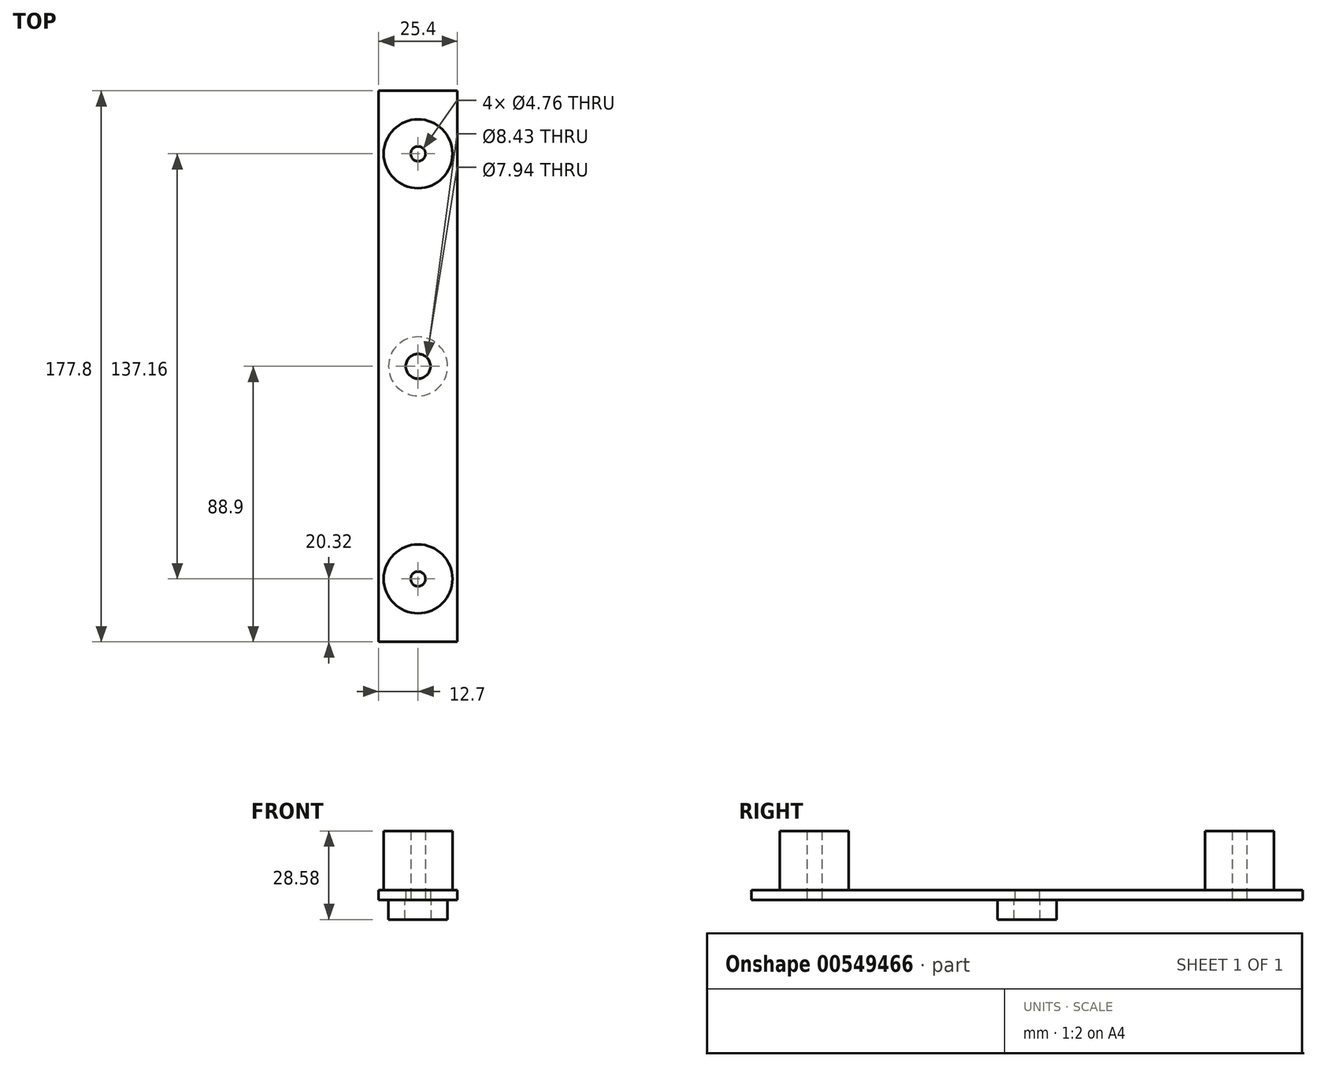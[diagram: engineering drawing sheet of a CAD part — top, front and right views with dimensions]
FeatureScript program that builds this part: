
annotation { "Feature Type Name" : "Feature", "Feature Type Description" : "" }
export const myFeature = defineFeature(function(context is Context, id is Id, definition is map)
    precondition{}
    {
        {
            var Q0;
            Q0=qCreatedBy(makeId("Top.planeOp"),FACE);
            var sketch = newSketch(context, id + "F0", { "sketchPlane" : qUnion([Q0])});
            skLineSegment(sketch, "E0.bottom", {"start": v(-12.7, 88.9) * mm, "end": v(12.7, 88.9) * mm});
            skLineSegment(sketch, "E0.top", {"start": v(-12.7, -88.9) * mm, "end": v(12.7, -88.9) * mm});
            skLineSegment(sketch, "E0.left", {"start": v(-12.7, 88.9) * mm, "end": v(-12.7, -88.9) * mm});
            skLineSegment(sketch, "E0.right", {"start": v(12.7, 88.9) * mm, "end": v(12.7, -88.9) * mm});
            skPoint(sketch, "E0.middle", {"position": v(0, 0) * mm});
            skPoint(sketch, "E1", {"position": v(0, -68.58) * mm});
            skPoint(sketch, "E2.MirrorP", {"position": v(0, 68.58) * mm});
            skCircle(sketch, "E3", {"center": v(0, -68.58) * mm, "radius": 2.38 * mm});
            skCircle(sketch, "E4.MirrorC", {"center": v(0, 68.58) * mm, "radius": 2.38 * mm});
            skCircle(sketch, "E5", {"center": v(0, 0) * mm, "radius": 3.97 * mm});
            skSolve(sketch);
        }
        {
            var Q0;
            Q0=makeQuery(id+"F0.imprint","IMPRINT",FACE,{"disambiguationData":[TD([[makeQuery(id+"F0.imprint","IMPRINT",EDGE,{"derivedFrom":sQuery(id+"F0.wireOp",EDGE,"E0.bottom")}),-1.0]])]});
            extrude(context, id + "F1", {"entities" : qUnion([Q0]), "depth" : 3.17 * mm, "offsetDistance" : 25.4 * mm});
        }
        {
            var Q0;
            Q0=makeQuery(id+"F1.opExtrude","CAP_FACE",FACE,{"disambiguationData":[OSD([sQuery(id+"F0.wireOp",EDGE,"E0.bottom"),sQuery(id+"F0.wireOp",EDGE,"E0.top"),sQuery(id+"F0.wireOp",EDGE,"E0.left"),sQuery(id+"F0.wireOp",EDGE,"E0.right")])],"isStart":true});
            var sketch = newSketch(context, id + "F2", { "sketchPlane" : qUnion([Q0])});
            skCircle(sketch, "E6.0", {"center": v(0, 0) * mm, "radius": 4.22 * mm});
            skCircle(sketch, "E7", {"center": v(0, 0) * mm, "radius": 9.53 * mm});
            skCircle(sketch, "E8", {"center": v(0, 0) * mm, "radius": 4.1 * mm});
            skCircle(sketch, "E9.0", {"center": v(0, 0) * mm, "radius": 3.97 * mm});
            skSolve(sketch);
        }
        {
            var Q0;
            Q0=makeQuery(id+"F2.imprint","IMPRINT",FACE,{"disambiguationData":[TD([[makeQuery(id+"F2.imprint","IMPRINT",EDGE,{"derivedFrom":sQuery(id+"F2.wireOp",EDGE,"E7")}),1.0]])]});
            extrude(context, id + "F3", {"entities" : qUnion([Q0]), "depth" : 6.35 * mm, "offsetDistance" : 25.4 * mm});
        }
        {
            var Q0;
            Q0=makeQuery(id+"F1.opExtrude","CAP_FACE",FACE,{"disambiguationData":[OSD([sQuery(id+"F0.wireOp",EDGE,"E0.bottom"),sQuery(id+"F0.wireOp",EDGE,"E0.top"),sQuery(id+"F0.wireOp",EDGE,"E0.left"),sQuery(id+"F0.wireOp",EDGE,"E0.right"),sQuery(id+"F0.wireOp",EDGE,"E3"),sQuery(id+"F0.wireOp",EDGE,"E4.MirrorC"),sQuery(id+"F0.wireOp",EDGE,"E5")])],"isStart":false});
            var sketch = newSketch(context, id + "F4", { "sketchPlane" : qUnion([Q0])});
            skCircle(sketch, "E10", {"center": v(0, -68.58) * mm, "radius": 11.11 * mm});
            skCircle(sketch, "E11", {"center": v(0, -68.58) * mm, "radius": 2.38 * mm});
            skCircle(sketch, "E12.MirrorC", {"center": v(0, 68.58) * mm, "radius": 11.11 * mm});
            skCircle(sketch, "E13.MirrorC", {"center": v(0, 68.58) * mm, "radius": 2.38 * mm});
            skSolve(sketch);
        }
        {
            var Q0;
            Q0=makeQuery(id+"F4.imprint","IMPRINT",FACE,{"disambiguationData":[TD([[makeQuery(id+"F4.imprint","IMPRINT",EDGE,{"derivedFrom":sQuery(id+"F4.wireOp",EDGE,"E10")}),1.0]])]});
            extrude(context, id + "F5", {"entities" : qUnion([Q0]), "depth" : 19.05 * mm, "offsetDistance" : 25.4 * mm});
        }
        {
            var Q0;
            Q0=makeQuery(id+"F5.opExtrude","SWEPT_BODY",BODY,{"disambiguationData":[OSD([sQuery(id+"F4.wireOp",EDGE,"E10"),sQuery(id+"F4.wireOp",EDGE,"E11")])]});
            var Q1;
            Q1=qCreatedBy(makeId("Front.planeOp"),FACE);
            mirror(context, id + "F6", {"entities" : qUnion([Q0]), "mirrorPlane" : qUnion([Q1])});
        }
    });
